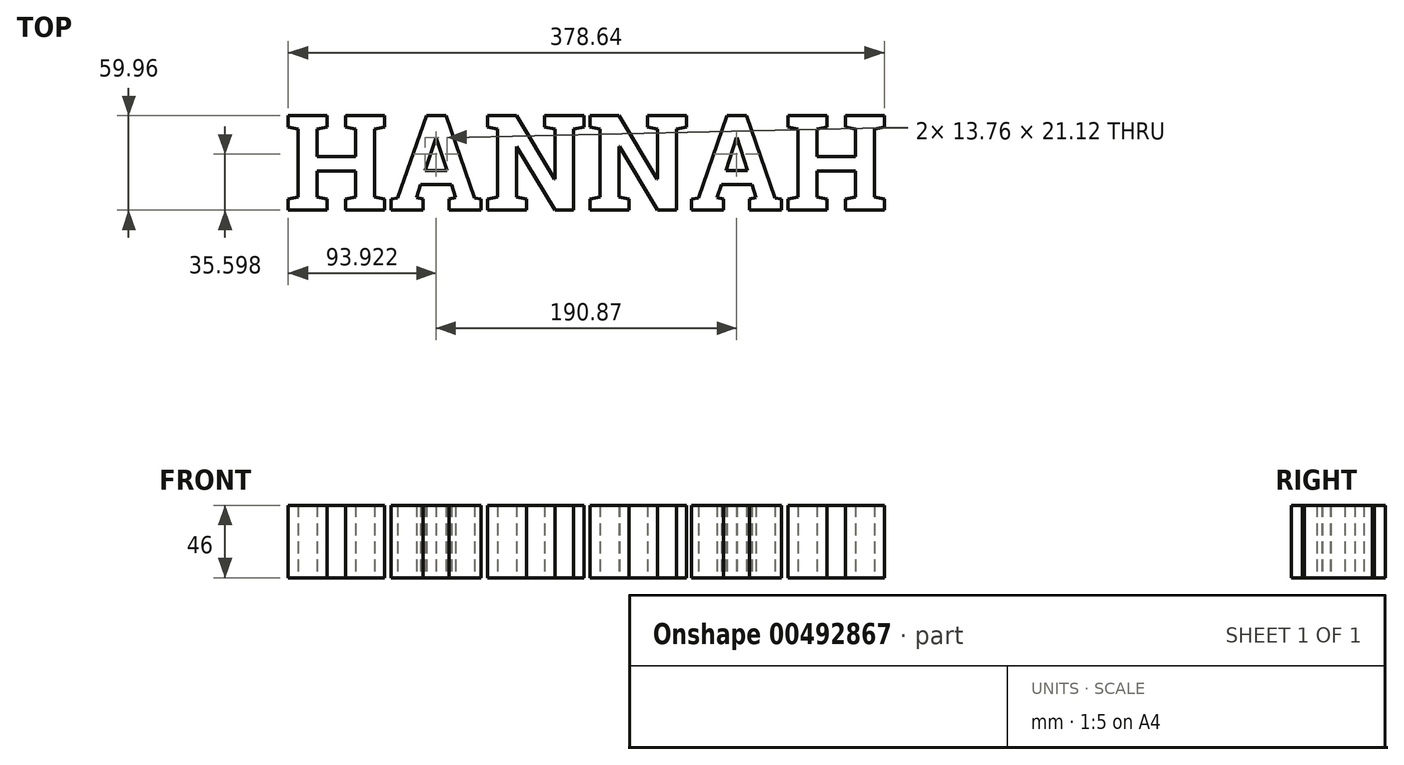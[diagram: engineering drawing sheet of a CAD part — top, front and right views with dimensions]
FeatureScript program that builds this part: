
annotation { "Feature Type Name" : "Feature", "Feature Type Description" : "" }
export const myFeature = defineFeature(function(context is Context, id is Id, definition is map)
    precondition{}
    {
        {
            var Q0;
            Q0=qCreatedBy(makeId("Top.planeOp"),FACE);
            var sketch = newSketch(context, id + "F0", { "sketchPlane" : qUnion([Q0])});
            skText(sketch, "E0", { "text": "HANNAH", "fontName": "RobotoSlab-Bold.ttf"});
            const initialGuessF0  = {"E0": [-0.12453, -0.0147, 1, 0, 0.06072]};
            skSetInitialGuess(sketch, initialGuessF0);
            skSolve(sketch);
        }
        {
            var Q0;
            Q0 = qSketchRegion(id + "F0", true);
            extrude(context, id + "F1", {"entities" : qUnion([Q0]), "depth" : 46 * mm});
        }
    });
